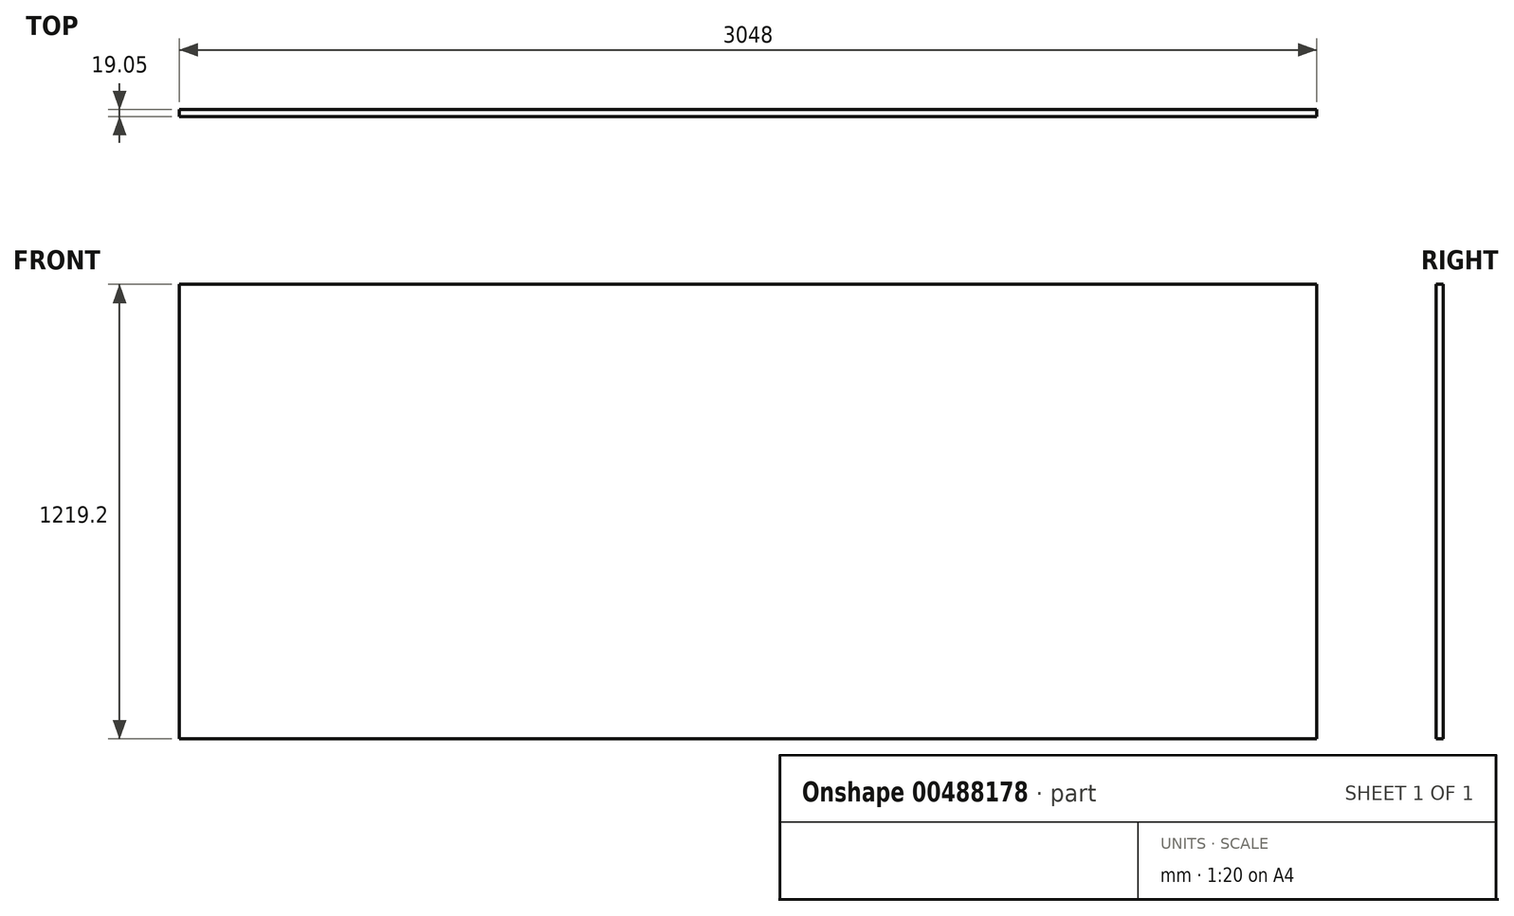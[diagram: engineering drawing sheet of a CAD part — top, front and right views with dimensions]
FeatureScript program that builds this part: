
annotation { "Feature Type Name" : "Feature", "Feature Type Description" : "" }
export const myFeature = defineFeature(function(context is Context, id is Id, definition is map)
    precondition{}
    {
        {
            var Q0;
            Q0=qCreatedBy(makeId("Front.planeOp"),FACE);
            var sketch = newSketch(context, id + "F0", { "sketchPlane" : qUnion([Q0])});
            skLineSegment(sketch, "E0", {"start": v(0, 0) * mm, "end": v(0, 1219.2) * mm});
            skLineSegment(sketch, "E1", {"start": v(0, 1219.2) * mm, "end": v(3048, 1219.2) * mm});
            skLineSegment(sketch, "E2", {"start": v(3048, 1219.2) * mm, "end": v(3048, 0) * mm});
            skLineSegment(sketch, "E3", {"start": v(3048, 0) * mm, "end": v(0, 0) * mm});
            skLineSegment(sketch, "E4", {"start": v(0, 0) * mm, "end": v(0, 0) * mm});
            skSolve(sketch);
        }
        {
            var Q0;
            Q0=makeQuery(id+"F0.imprint","IMPRINT",FACE,{"disambiguationData":[TD([[makeQuery(id+"F0.imprint","IMPRINT",EDGE,{"derivedFrom":sQuery(id+"F0.wireOp",EDGE,"E0")}),-1.0]])]});
            extrude(context, id + "F1", {"entities" : qUnion([Q0]), "depth" : 19.05 * mm, "offsetDistance" : 25.4 * mm});
        }
    });
